# Revit family: 61HD 3 inch Vert Dsc
name_source: partatom
category: Mechanical Equipment
revit_build: Autodesk Revit 2013 (Build: 20120221_2030(x64)
units: mm (PartAtom-declared; Revit-internal decimal feet)

## types (42) — shared parameters
Assembly Code = D2010900
Default Elevation = 0"
Description = Commercial Effluent Pumps
Discharge Diameter = 3"
Discharge Radius = 1 1/2"
Flange = ANSI B16.1
Height = 29 1/4"
Hertz = 60
Impeller Type (Optional) = Ductile Iron Vortex
Installation Type = Floor Mounted
Insulation = Class F
Lead Wires Insulation = Class F
Length = 17 9/16"
Manufacturer = Zoeller
Masterformat Number = 33 36 16
Masterformat Title = Utility Septic Tank Effluent Pumps
Material = Cast Iron-Zoeller-Powder Coated Epoxy
Max. Stator Temp. = 311 °F
Max. Water Temp. = 104 °F
Min. Recommended Fluid Level = 24"
Moisture Sensor (Optional) = Moisture Sensing Probes (Requires a circuit in control panel)
Motor Design Letter = NEMA B
Motor Shaft = 416 S.S.
Motor Thermal Shutoff (Single Phase Only) = Thermal Sensors With Automatic Reset
O-Rings and Cover Gasket = Buna-N
Omniclass Table 23 Code = 23.60.30.21
Omniclass Table 23 Title = Pumps
Operation = Non-Automatic
Power Cord = #12-4 SO (Models with a FLA greater than 20 amps use #8-4 gauge power cord)
Price = Prices may vary. Please consult Manufacturer Representative for most up-to-date price list.
Product Page URL = http://www.zoellerengprod.com
Shaft Seal Lower (Options) = Carbon/Silicon Carbide, Silicon Carbide/Silicon Carbide
Shaft Seal Lower Standard = Silicon Carbide/Carbon
Shaft Seal Upper (Options) = Silicon Carbide/Carbon, Silicon Carbide/Silicon Carbide
Shaft Seal Upper Standard = Carbon/Ceramic
Shipping Weight = 245 lbs (111 kg)
Solid Size = 2 1/2" (64 mm)
Tandem Seals = Standard
Type SOW Power Cord Length = 300"
URL = http://www.zoellerengprod.com
Warranty Information = 36 Months (Limited)
Waste Connection = Yes
Width = 12 5/8"

## per-type parameters (varying)
| type | Apparent Load | Dry Pit (1-3 BHP, Intermittent Duty) | Flow @ 5' | Full Load Amps | High Temp (1-3 BHP Only) | Impeller Diameter | Impeller Type | Inverter Duty Submersible (1-5 BHP Only) | Locked Rotor Amps (Voltage Dependant) | Maximum KW Input | Model | Motor | Motor Type | NEC Locked Rotor Code | Phase | RPM | Service Factor | Type | Voltage |
| 6111-3" 230V 1Ph | 6440 VA | No | 470 GPM | 28 A | No | 4 3/8" | Bronze Semi-Open | Yes | 132.0 | 5.3 | 6111-3" | 5.0 BHP | Submersible | E | 1 | 3450 | 1.2 | Permanent Split Capacitor | 230 V |
| 6111-3" 200V 3Ph | 3500 VA | No | 470 GPM | 18 A | No | 4 3/8" | Bronze Semi-Open | Yes | 66.0 | 5.3 | 6111-3" | 5.0 BHP | Submersible | E | 3 | 3450 | 1.2 | 3Ph | 200 V |
| 6111-3" 230V 3Ph | 3496 VA | No | 470 GPM | 15 A | No | 4 3/8" | Bronze Semi-Open | Yes | 57.0 | 5.3 | 6111-3" | 5.0 BHP | Submersible | E | 3 | 3450 | 1.2 | 3Ph | 230 V |
| 6111-3" 460V 3Ph | 3496 VA | No | 470 GPM | 8 A | No | 4 3/8" | Bronze Semi-Open | Yes | 28.50 | 5.3 | 6111-3" | 5.0 BHP | Submersible | E | 3 | 3450 | 1.2 | 3Ph | 460 V |
| 6111-3" 575V 3Ph | 3507 VA | No | 470 GPM | 6 A | No | 4 3/8" | Bronze Semi-Open | Yes | 25.20 | 5.3 | 6111-3" | 5.0 BHP | Submersible | E | 3 | 3450 | 1.2 | 3Ph | 575 V |
| 6112-3" 200V 3Ph | 5060 VA | No | 550 GPM | 25 A | No | 4 3/4" | Bronze Semi-Open | No | 66.0 | 7.8 | 6112-3" | 7.5 BHP | Submersible | D | 3 | 3450 | 1.2 | 3 Phase | 200 V |
| 6112-3" 230V 3Ph | 5060 VA | No | 550 GPM | 22 A | No | 4 3/4" | Bronze Semi-Open | No | 82.0 | 7.8 | 6112-3" | 7.5 BHP | Submersible | D | 3 | 3450 | 1.2 | 3 Phase | 230 V |
| 6112-3" 460V 3Ph | 5060 VA | No | 550 GPM | 11 A | No | 4 3/4" | Bronze Semi-Open | No | 41.0 | 7.8 | 6112-3" | 7.5 BHP | Submersible | D | 3 | 3450 | 1.2 | 3 Phase | 460 V |
| 6112-3" 575V 3Ph | 5175 VA | No | 550 GPM | 9 A | No | 4 3/4" | Bronze Semi-Open | No | 36.0 | 7.8 | 6112-3" | 7.5 BHP | Submersible | D | 3 | 3450 | 1.2 | 3 Phase | 575 V |
| 6113-3" 200V 3Ph | 6440 VA | No | 620 GPM | 32 A | No | 5 1/8" | Bronze Semi-Open | No | 94.0 | 10.5 | 6113-3" | 10.0 BHP | Submersible | B | 3 | 3450 | 1.0 | 3 Phase | 200 V |
| 6113-3" 230V 3Ph | 6440 VA | No | 620 GPM | 28 A | No | 5 1/8" | Bronze Semi-Open | No | 82.0 | 10.5 | 6113-3" | 10.0 BHP | Submersible | B | 3 | 3450 | 1.0 | 3 Phase | 230 V |
| 6113-3" 460V 3Ph | 6440 VA | No | 620 GPM | 14 A | No | 5 1/8" | Bronze Semi-Open | No | 41.0 | 10.5 | 6113-3" | 10.0 BHP | Submersible | B | 3 | 3450 | 1.0 | 3 Phase | 460 V |
| 6113-3" 575V 3Ph | 6325 VA | No | 620 GPM | 11 A | No | 5 1/8" | Bronze Semi-Open | No | 36.0 | 10.5 | 6113-3" | 10.0 BHP | Submersible | B | 3 | 3450 | 1.0 | 3 Phase | 575 V |
| 6120-3" 230V 1Ph | 1587 VA | Yes | 250 GPM | 7 A | Yes | 4 7/8" | Ductile Iron Semi-Open | Yes | 48.0 | 1.4 | 6120-3" | 1.0 BHP | Standard Submersible | M | 1 | 1750 | 1.2 | Permanent Split Capacitor | 230 V |
| 6120-3" 200V 3Ph | 860 VA | Yes | 250 GPM | 4 A | Yes | 4 7/8" | Ductile Iron Semi-Open | Yes | 32.0.0 | 1.4 | 6120-3" | 1.0 BHP | Standard Submersible | M | 3 | 1750 | 1.2 | 3 Phase | 200 V |
| 6120-3" 230V 3Ph | 851 VA | Yes | 250 GPM | 4 A | Yes | 4 7/8" | Ductile Iron Semi-Open | Yes | 28.0 | 1.4 | 6120-3" | 1.0 BHP | Standard Submersible | M | 3 | 1750 | 1.2 | 3 Phase | 230 V |
| 6120-3" 460V 3Ph | 874 VA | Yes | 250 GPM | 2 A | Yes | 4 7/8" | Ductile Iron Semi-Open | Yes | 14.0 | 1.4 | 6120-3" | 1.0 BHP | Standard Submersible | M | 3 | 1750 | 1.2 | 3 Phase | 460 V |
| 6120-3" 575V 3Ph | 920 VA | Yes | 250 GPM | 2 A | Yes | 4 7/8" | Ductile Iron Semi-Open | Yes | 11.5 | 1.4 | 6120-3" | 1.0 BHP | Standard Submersible | M | 3 | 1750 | 1.2 | 3 Phase | 575 V |
| 6121-3" 230V 1Ph | 0 VA | Yes | 320 GPM | 9 A | Yes | 5 3/8" | Ductile Iron Semi-Open | Yes | 48.0 | 1.9 | 6121-3" | 1.5 BHP | Standard Submersible | J | 1 | 1750 | 1.2 | Permanent Split Capacitor | 230 V |
| 6121-3" 200V 3Ph | 1180 VA | Yes | 320 GPM | 6 A | Yes | 5 3/8" | Ductile Iron Semi-Open | Yes | 32.0 | 1.9 | 6121-3" | 1.5 BHP | Standard Submersible | J | 1 | 1750 | 1.2 | Permanent Split Capacitor | 200 V |
| 6121-3" 230V 3Ph | 1173 VA | Yes | 320 GPM | 5 A | Yes | 5 3/8" | Ductile Iron Semi-Open | Yes | 28.0 | 1.9 | 6121-3" | 1.5 BHP | Standard Submersible | J | 1 | 1750 | 1.2 | Permanent Split Capacitor | 230 V |
| 6121-3" 460V 3Ph | 1196 VA | Yes | 320 GPM | 3 A | Yes | 5 3/8" | Ductile Iron Semi-Open | Yes | 14.0 | 1.9 | 6121-3" | 1.5 BHP | Standard Submersible | J | 1 | 1750 | 1.2 | Permanent Split Capacitor | 460 V |
| 6121-3" 575V 3Ph | 1150 VA | Yes | 320 GPM | 2 A | Yes | 5 3/8" | Ductile Iron Semi-Open | Yes | 11.5 | 1.9 | 6121-3" | 1.5 BHP | Standard Submersible | J | 1 | 1750 | 1.2 | Permanent Split Capacitor | 575 V |
| 6122-3" 230V 1Ph | 3335 VA | Yes | 390 GPM | 15 A | Yes | 5 3/4" | Ductile Iron Semi-Open | Yes | 86.0 | 2.4 | 6122-3" | 2.0 BHP | Standard Submersible | K | 1 | 1750 | 1.2 | Permanent Split Capacitor | 230 V |
| 6122-3" 200V 3Ph | 1560 VA | Yes | 380 GPM | 8 A | Yes | 5 3/4" | Ductile Iron Semi-Open | Yes | 46.0 | 2.4 | 6122-3" | 2.0 BHP | Standard Submersible | K | 3 | 1750 | 1.2 | 3 Phase | 200 V |
| 6122-3" 230V 3Ph | 1564 VA | Yes | 380 GPM | 7 A | Yes | 5 3/4" | Ductile Iron Semi-Open | Yes | 41.0 | 2.4 | 6122-3" | 2.0 BHP | Standard Submersible | K | 3 | 1750 | 1.2 | 3 Phase | 230 V |
| 6122-3" 460V 3Ph | 1564 VA | Yes | 380 GPM | 3 A | Yes | 5 3/4" | Ductile Iron Semi-Open | Yes | 20.5 | 2.4 | 6122-3" | 2.0 BHP | Standard Submersible | K | 3 | 1750 | 1.2 | 3 Phase | 460 V |
| 6122-3" 575V 3Ph | 1553 VA | Yes | 380 GPM | 3 A | Yes | 5 3/4" | Ductile Iron Semi-Open | Yes | 16.2 | 2.4 | 6122-3" | 2.0 BHP | Standard Submersible | K | 3 | 1750 | 1.2 | 3 Phase | 575 V |
| 6123-3" 230V 1Ph | 3910 VA | Yes | 450 GPM | 17 A | Yes | 6 3/8" | Ductile Iron Semi-Open | Yes | 86.0 | 3.5 | 6123-3" | 3.0 BHP | Standard Submersible | F | 1 | 1750 | 1.2 | Permanent Split Capacitor | 230 V |
| 6123-3" 200V 3Ph | 2200 VA | Yes | 420 GPM | 11 A | Yes | 6 3/8" | Ductile Iron Semi-Open | Yes | 46.0 | 3.5 | 6123-3" | 3.0 BHP | Standard Submersible | F | 3 | 1750 | 1.2 | 3 Phase | 200 V |
| 6123-3" 230V 3Ph | 2208 VA | Yes | 450 GPM | 10 A | Yes | 6 3/8" | Ductile Iron Semi-Open | Yes | 41.0 | 3.5 | 6123-3" | 3.0 BHP | Standard Submersible | F | 3 | 1750 | 1.2 | 3 Phase | 230 V |
| 6123-3" 460V 3Ph | 2208 VA | Yes | 450 GPM | 5 A | Yes | 6 3/8" | Ductile Iron Semi-Open | Yes | 20.5 | 3.5 | 6123-3" | 3.0 BHP | Standard Submersible | F | 3 | 1750 | 1.2 | 3 Phase | 460 V |
| 6123-3" 575V 3Ph | 2243 VA | Yes | 450 GPM | 4 A | Yes | 6 3/8" | Ductile Iron Semi-Open | Yes | 16.2 | 3.5 | 6123-3" | 3.0 BHP | Standard Submersible | F | 3 | 1750 | 1.2 | 3 Phase | 575 V |
| 6124-3" 230V 1Ph | 6440 VA | No | 475 GPM | 28 A | No | 7" | Ductile Iron Semi-Open | Yes | 139.0 | 5.5 | 6124-3" | 5.0 BHP | Standard Submersible | E | 1 | 1750 | 1.2 | Permanent Split Capacitor | 230 V |
| 6124-3" 200V 3Ph | 3500 VA | No | 530 GPM | 18 A | No | 7" | Ductile Iron Semi-Open | Yes | 64.0 | 5.5 | 6124-3" | 5.0 BHP | Standard Submersible | E | 3 | 1750 | 1.2 | 3 Phase | 200 V |
| 6124-3" 230V 3Ph | 3496 VA | No | 530 GPM | 15 A | No | 7" | Ductile Iron Semi-Open | Yes | 58.0 | 5.5 | 6124-3" | 5.0 BHP | Standard Submersible | E | 3 | 1750 | 1.2 | 3 Phase | 230 V |
| 6124-3" 460V 3Ph | 3496 VA | No | 530 GPM | 8 A | No | 7" | Ductile Iron Semi-Open | Yes | 29.0 | 5.5 | 6124-3" | 5.0 BHP | Standard Submersible | E | 3 | 1750 | 1.2 | 3 Phase | 460 V |
| 6124-3" 575V 3Ph | 3508 VA | No | 530 GPM | 6 A | No | 7" | Ductile Iron Semi-Open | Yes | 23.0 | 5.5 | 6124-3" | 5.0 BHP | Standard Submersible | E | 3 | 1750 | 1.2 | 3 Phase | 575 V |
| 6125-3" 200V 3Ph | 5060 VA | No | 600 GPM | 25 A | No | 7 1/2" | Ductile Iron Semi-Open | No | 83.0 | 6.9 | 6125-3" | 7.5 BHP | Standard Submersible | C | 3 | 1750 | 1.0 | 3 Phase | 200 V |
| 6125-3" 230V 3Ph | 5060 VA | No | 600 GPM | 22 A | No | 7 1/2" | Ductile Iron Semi-Open | No | 72.0 | 6.9 | 6125-3" | 7.5 BHP | Standard Submersible | C | 3 | 1750 | 1.0 | 3 Phase | 230 V |
| 6125-3" 460V 3Ph | 5060 VA | No | 600 GPM | 11 A | No | 7 1/2" | Ductile Iron Semi-Open | No | 36.0 | 6.9 | 6125-3" | 7.5 BHP | Standard Submersible | C | 3 | 1750 | 1.0 | 3 Phase | 460 V |
| 6125-3" 575V 3Ph | 5175 VA | No | 600 GPM | 9 A | No | 7 1/2" | Ductile Iron Semi-Open | No | 29.0 | 6.9 | 6125-3" | 7.5 BHP | Standard Submersible | C | 3 | 1750 | 1.0 | 3 Phase | 575 V |

## geometry (parser evidence)
native form markers: Blend x6, Sweep x1
no freeform markers — native parametric forms only
